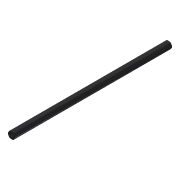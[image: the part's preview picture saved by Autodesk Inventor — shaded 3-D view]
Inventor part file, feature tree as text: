
AUTODESK INVENTOR PART (.ipt)
format: ipt  version: 2015 (Build 190159000, 159)  size: 82,432 bytes
history: native  units: in
note: dims shown in document units (in); Inventor stores cm internally (conversion verified against a paired STEP export)
features: other x3, extrude x1, sketch x1
ambient origin geometry x8: Origin, YZ Plane, XZ Plane, XY Plane, X Axis, Y Axis, Z Axis, Center Point
bodies: Solid1 (feature_tree)
feature tree (5):
  other  "Blocks"
  extrude  "Extrusion1"  [1 undecoded]
  sketch  "Sketch1"  dims[d0=12.0in d1=0.0in]
  other  "ThunderHex"
  other  "ThunderHex:1"
note: 1 required parameter value undecoded (feature->parameter linkage not recoverable at this tier; creation-order binding heuristic only, values carry confidence <= 0.55)
